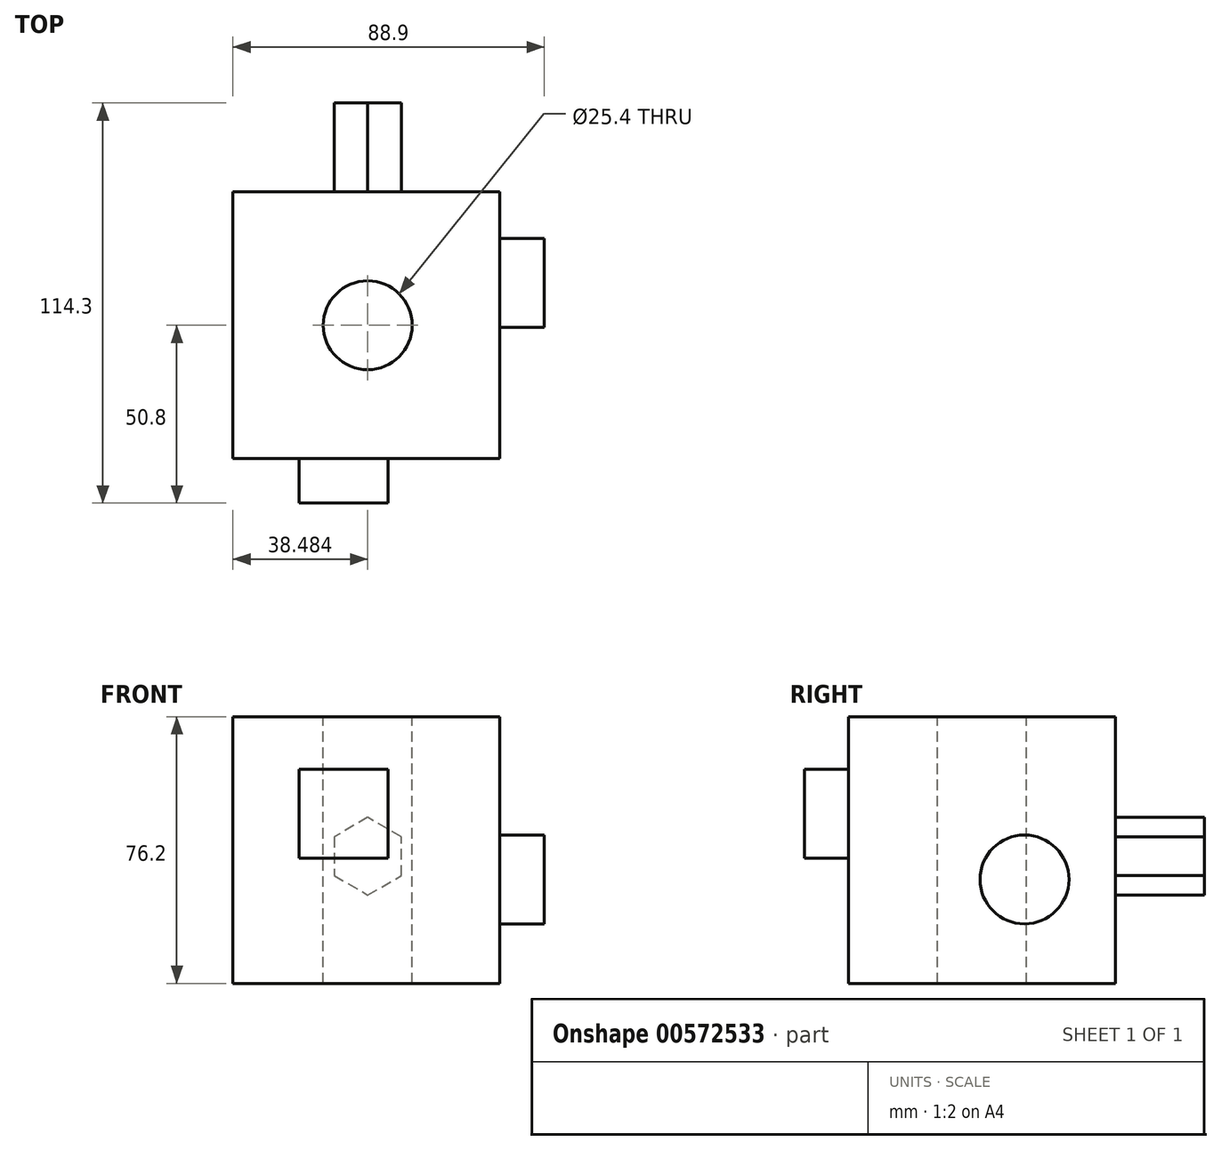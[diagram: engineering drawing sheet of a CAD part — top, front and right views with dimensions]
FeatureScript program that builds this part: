
annotation { "Feature Type Name" : "Feature", "Feature Type Description" : "" }
export const myFeature = defineFeature(function(context is Context, id is Id, definition is map)
    precondition{}
    {
        {
            var Q0;
            Q0=qCreatedBy(makeId("Front.planeOp"),FACE);
            var sketch = newSketch(context, id + "F0", { "sketchPlane" : qUnion([Q0])});
            skLineSegment(sketch, "E0.bottom", {"start": v(0, 152.4) * mm, "end": v(76.2, 152.4) * mm});
            skLineSegment(sketch, "E0.top", {"start": v(0, 76.2) * mm, "end": v(76.2, 76.2) * mm});
            skLineSegment(sketch, "E0.left", {"start": v(0, 152.4) * mm, "end": v(0, 76.2) * mm});
            skLineSegment(sketch, "E0.right", {"start": v(76.2, 152.4) * mm, "end": v(76.2, 76.2) * mm});
            skSolve(sketch);
        }
        {
            var Q0;
            Q0=makeQuery(id+"F0.imprint","IMPRINT",FACE,{"disambiguationData":[TD([[makeQuery(id+"F0.imprint","IMPRINT",EDGE,{"derivedFrom":sQuery(id+"F0.wireOp",EDGE,"E0.bottom")}),-1.0]])]});
            extrude(context, id + "F1", {"entities" : qUnion([Q0]), "depth" : 76.2 * mm, "offsetDistance" : 25.4 * mm});
        }
        {
            var Q0;
            Q0=makeQuery(id+"F1.opExtrude","SWEPT_FACE",FACE,{"disambiguationData":[OSD([sQuery(id+"F0.wireOp",EDGE,"E0.bottom")])]});
            var sketch = newSketch(context, id + "F2", { "sketchPlane" : qUnion([Q0])});
            skCircle(sketch, "E1", {"center": v(38.48, -38.1) * mm, "radius": 19.05 * mm});
            skPoint(sketch, "E1.centerSnap0", {"position": v(0, -38.1) * mm});
            skSolve(sketch);
        }
        {
            var Q0;
            Q0=sQuery(id+"F2.wireOp",VERTEX,"E1.center");
            var Q1;
            Q1=makeQuery(id+"F1.opExtrude","SWEPT_BODY",BODY,{"disambiguationData":[OSD([sQuery(id+"F0.wireOp",EDGE,"E0.bottom"),sQuery(id+"F0.wireOp",EDGE,"E0.top"),sQuery(id+"F0.wireOp",EDGE,"E0.left"),sQuery(id+"F0.wireOp",EDGE,"E0.right")])]});
            hole(context, id + "F3", {"style" : HoleStyle.SIMPLE, "endStyle" : HoleEndStyle.THROUGH, "holeDiameter" : 25.4 * mm, "isTappedThrough" : true, "tappedDepth" : 12.7 * mm, "tapClearance" : 3, "locations" : qUnion([Q0]), "scope" : qUnion([Q1])});
        }
        {
            var Q0;
            Q0=makeQuery(id+"F1.opExtrude","CAP_FACE",FACE,{"disambiguationData":[OSD([sQuery(id+"F0.wireOp",EDGE,"E0.bottom"),sQuery(id+"F0.wireOp",EDGE,"E0.top"),sQuery(id+"F0.wireOp",EDGE,"E0.left"),sQuery(id+"F0.wireOp",EDGE,"E0.right")])],"isStart":false});
            var sketch = newSketch(context, id + "F4", { "sketchPlane" : qUnion([Q0])});
            skLineSegment(sketch, "E2.bottom", {"start": v(18.92, 137.33) * mm, "end": v(44.32, 137.33) * mm});
            skLineSegment(sketch, "E2.top", {"start": v(18.92, 111.93) * mm, "end": v(44.32, 111.93) * mm});
            skLineSegment(sketch, "E2.left", {"start": v(18.92, 137.33) * mm, "end": v(18.92, 111.93) * mm});
            skLineSegment(sketch, "E2.right", {"start": v(44.32, 137.33) * mm, "end": v(44.32, 111.93) * mm});
            skSolve(sketch);
        }
        {
            var Q0;
            Q0=makeQuery(id+"F4.imprint","IMPRINT",FACE,{"disambiguationData":[TD([[makeQuery(id+"F4.imprint","IMPRINT",EDGE,{"derivedFrom":sQuery(id+"F4.wireOp",EDGE,"E2.bottom")}),-1.0]])]});
            extrude(context, id + "F5", {"entities" : qUnion([Q0]), "operationType" : NewBodyOperationType.ADD, "depth" : 12.7 * mm, "offsetDistance" : 25.4 * mm});
        }
        {
            var Q0;
            Q0=makeQuery(id+"F1.opExtrude","SWEPT_FACE",FACE,{"disambiguationData":[OSD([sQuery(id+"F0.wireOp",EDGE,"E0.right")])]});
            var sketch = newSketch(context, id + "F6", { "sketchPlane" : qUnion([Q0])});
            skCircle(sketch, "E3", {"center": v(-26.03, 105.9) * mm, "radius": 12.7 * mm});
            skSolve(sketch);
        }
        {
            var Q0;
            Q0=makeQuery(id+"F6.imprint","IMPRINT",FACE,{"disambiguationData":[TD([[makeQuery(id+"F6.imprint","IMPRINT",EDGE,{"derivedFrom":sQuery(id+"F6.wireOp",EDGE,"E3")}),1.0]])]});
            extrude(context, id + "F7", {"entities" : qUnion([Q0]), "operationType" : NewBodyOperationType.ADD, "depth" : 12.7 * mm, "offsetDistance" : 25.4 * mm});
        }
        {
            var Q0;
            Q0=makeQuery(id+"F1.opExtrude","CAP_FACE",FACE,{"disambiguationData":[OSD([sQuery(id+"F0.wireOp",EDGE,"E0.bottom"),sQuery(id+"F0.wireOp",EDGE,"E0.top"),sQuery(id+"F0.wireOp",EDGE,"E0.left"),sQuery(id+"F0.wireOp",EDGE,"E0.right")])],"isStart":true});
            var sketch = newSketch(context, id + "F8", { "sketchPlane" : qUnion([Q0])});
            skCircle(sketch, "E4.cCircle", {"center": v(-38.5, 112.53) * mm, "radius": 9.6 * mm, "construction": true});
            skLineSegment(sketch, "E4.0", {"start": v(-28.91, 118.07) * mm, "end": v(-28.91, 107) * mm});
            skLineSegment(sketch, "E4.1", {"start": v(-28.91, 107) * mm, "end": v(-38.5, 101.46) * mm});
            skLineSegment(sketch, "E4.2", {"start": v(-38.5, 101.46) * mm, "end": v(-48.1, 107) * mm});
            skLineSegment(sketch, "E4.3", {"start": v(-48.1, 107) * mm, "end": v(-48.1, 118.07) * mm});
            skLineSegment(sketch, "E4.4", {"start": v(-48.1, 118.07) * mm, "end": v(-38.5, 123.6) * mm});
            skLineSegment(sketch, "E4.5", {"start": v(-38.5, 123.6) * mm, "end": v(-28.91, 118.07) * mm});
            skPoint(sketch, "E4.0.midPoint", {"position": v(-28.91, 112.53) * mm});
            skSolve(sketch);
        }
        {
            var Q0;
            Q0=makeQuery(id+"F8.imprint","IMPRINT",FACE,{"disambiguationData":[TD([[makeQuery(id+"F8.imprint","IMPRINT",EDGE,{"derivedFrom":sQuery(id+"F8.wireOp",EDGE,"E4.0")}),-1.0]])]});
            extrude(context, id + "F9", {"entities" : qUnion([Q0]), "operationType" : NewBodyOperationType.ADD, "depth" : 25.4 * mm, "offsetDistance" : 25.4 * mm});
        }
    });
